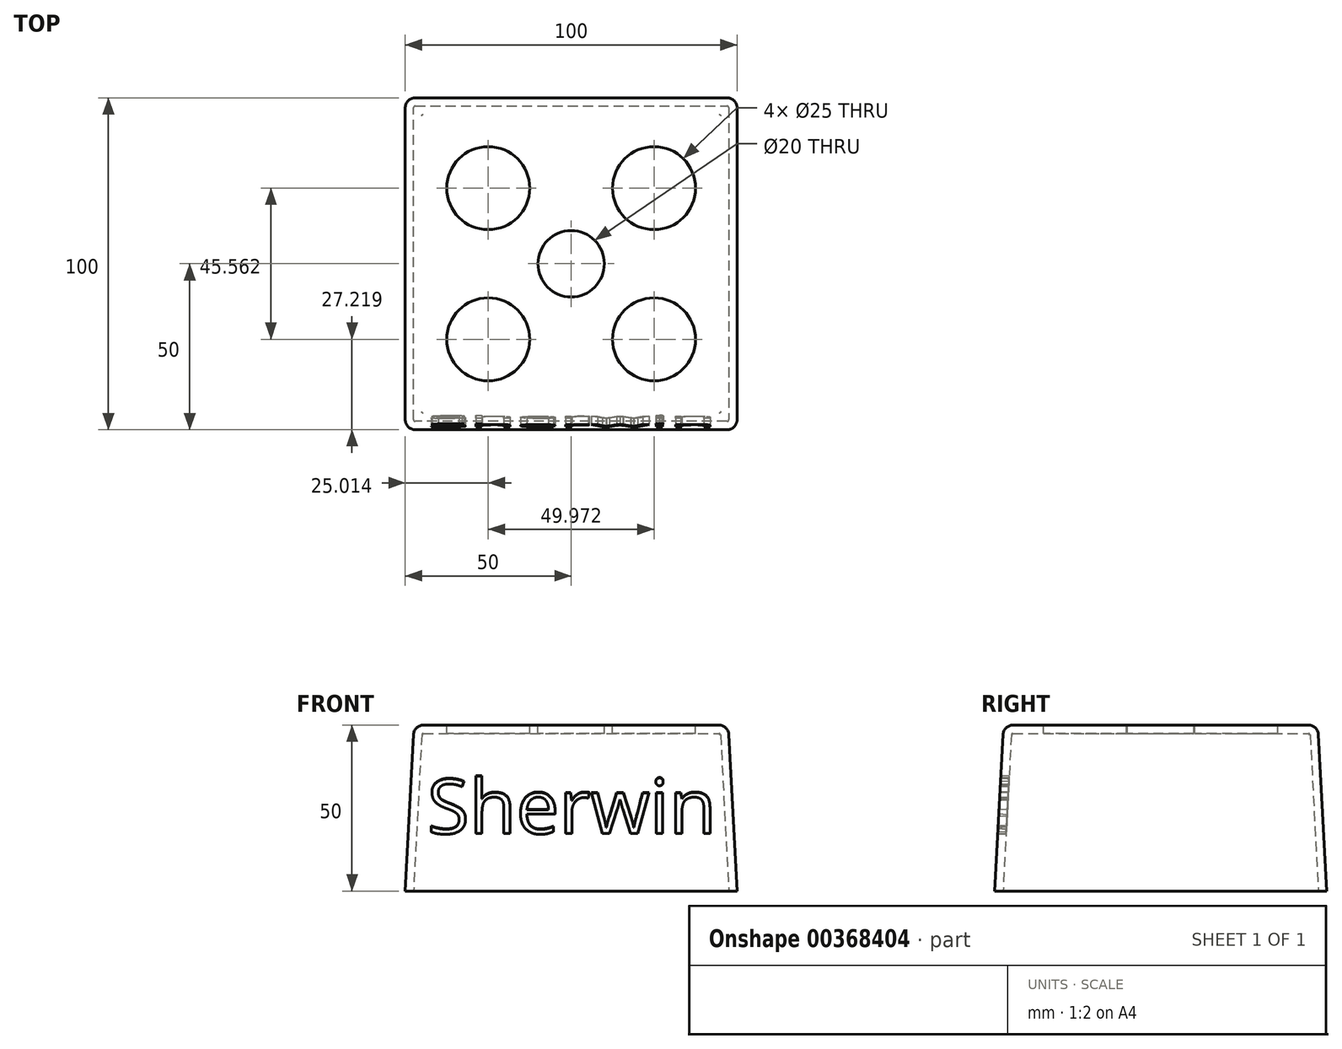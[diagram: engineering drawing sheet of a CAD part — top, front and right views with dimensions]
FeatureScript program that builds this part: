
annotation { "Feature Type Name" : "Feature", "Feature Type Description" : "" }
export const myFeature = defineFeature(function(context is Context, id is Id, definition is map)
    precondition{}
    {
        {
            var Q0;
            Q0=qCreatedBy(makeId("Top.planeOp"),FACE);
            var sketch = newSketch(context, id + "F0", { "sketchPlane" : qUnion([Q0])});
            skLineSegment(sketch, "E0.bottom", {"start": v(0, 0) * mm, "end": v(100, 0) * mm});
            skLineSegment(sketch, "E0.top", {"start": v(0, 100) * mm, "end": v(100, 100) * mm});
            skLineSegment(sketch, "E0.left", {"start": v(0, 0) * mm, "end": v(0, 100) * mm});
            skLineSegment(sketch, "E0.right", {"start": v(100, 0) * mm, "end": v(100, 100) * mm});
            skSolve(sketch);
        }
        {
            var Q0;
            Q0=makeQuery(id+"F0.imprint","IMPRINT",FACE,{"disambiguationData":[TD([[makeQuery(id+"F0.imprint","IMPRINT",EDGE,{"derivedFrom":sQuery(id+"F0.wireOp",EDGE,"E0.bottom")}),1.0]])]});
            extrude(context, id + "F1", {"entities" : qUnion([Q0]), "depth" : 50 * mm, "hasDraft" : true, "draftAngle" : 3 * degree, "draftPullDirection" : true});
        }
        {
            var Q0;
            Q0=makeQuery(id+"F1.opExtrude","SWEPT_EDGE",EDGE,{"disambiguationData":[OSD([sQuery(id+"F0.wireOp",EDGE,"E0.bottom"),sQuery(id+"F0.wireOp",EDGE,"E0.right")])]});
            var Q1;
            Q1=makeQuery(id+"F1.opExtrude","CAP_FACE",FACE,{"disambiguationData":[OSD([sQuery(id+"F0.wireOp",EDGE,"E0.bottom"),sQuery(id+"F0.wireOp",EDGE,"E0.top"),sQuery(id+"F0.wireOp",EDGE,"E0.left"),sQuery(id+"F0.wireOp",EDGE,"E0.right")])],"isStart":false});
            var Q2;
            Q2=makeQuery(id+"F1.opExtrude","SWEPT_EDGE",EDGE,{"disambiguationData":[OSD([sQuery(id+"F0.wireOp",EDGE,"E0.top"),sQuery(id+"F0.wireOp",EDGE,"E0.right")])]});
            var Q3;
            Q3=makeQuery(id+"F1.opExtrude","SWEPT_EDGE",EDGE,{"disambiguationData":[OSD([sQuery(id+"F0.wireOp",EDGE,"E0.bottom"),sQuery(id+"F0.wireOp",EDGE,"E0.left")])]});
            var Q4;
            Q4=makeQuery(id+"F1.opExtrude","SWEPT_EDGE",EDGE,{"disambiguationData":[OSD([sQuery(id+"F0.wireOp",EDGE,"E0.top"),sQuery(id+"F0.wireOp",EDGE,"E0.left")])]});
            fillet(context, id + "F2", {"entities" : qUnion([Q0, Q1, Q2, Q3, Q4]), "radius" : 3 * mm, "tangentPropagation" : true, "allowEdgeOverflow" : false});
        }
        {
            var Q0;
            Q0=makeQuery(id+"F1.opExtrude","CAP_FACE",FACE,{"disambiguationData":[OSD([sQuery(id+"F0.wireOp",EDGE,"E0.bottom"),sQuery(id+"F0.wireOp",EDGE,"E0.top"),sQuery(id+"F0.wireOp",EDGE,"E0.left"),sQuery(id+"F0.wireOp",EDGE,"E0.right")])],"isStart":true});
            shell(context, id + "F3", {"entities" : qUnion([Q0]), "thickness" : 2.5 * mm});
        }
        {
            var Q0;
            Q0=makeQuery(id+"F1.opExtrude","CAP_FACE",FACE,{"disambiguationData":[OSD([sQuery(id+"F0.wireOp",EDGE,"E0.bottom"),sQuery(id+"F0.wireOp",EDGE,"E0.top"),sQuery(id+"F0.wireOp",EDGE,"E0.left"),sQuery(id+"F0.wireOp",EDGE,"E0.right")])],"isStart":false});
            var sketch = newSketch(context, id + "F4", { "sketchPlane" : qUnion([Q0])});
            skCircle(sketch, "E1", {"center": v(50, 50) * mm, "radius": 10 * mm});
            skPoint(sketch, "E1.centerSnap0", {"position": v(5.47, 50) * mm});
            skPoint(sketch, "E1.centerSnap1", {"position": v(50, 94.53) * mm});
            skLineSegment(sketch, "E2", {"start": v(5.47, 50) * mm, "end": v(94.53, 50) * mm, "construction": true});
            skLineSegment(sketch, "E3", {"start": v(50, 94.53) * mm, "end": v(50, 5.47) * mm, "construction": true});
            skCircle(sketch, "E4", {"center": v(25.01, 72.78) * mm, "radius": 12.5 * mm});
            skCircle(sketch, "E5", {"center": v(25.01, 27.22) * mm, "radius": 12.5 * mm});
            skCircle(sketch, "E6", {"center": v(74.99, 27.22) * mm, "radius": 12.5 * mm});
            skCircle(sketch, "E7", {"center": v(74.99, 72.78) * mm, "radius": 12.5 * mm});
            skCircle(sketch, "E8", {"center": v(23, 50) * mm, "radius": 5 * mm});
            skSolve(sketch);
        }
        {
            var Q0;
            Q0=makeQuery(id+"F4.imprint","IMPRINT",FACE,{"disambiguationData":[TD([[makeQuery(id+"F4.imprint","IMPRINT",EDGE,{"derivedFrom":sQuery(id+"F4.wireOp",EDGE,"E1")}),1.0]])]});
            extrude(context, id + "F5", {"entities" : qUnion([Q0]), "operationType" : NewBodyOperationType.REMOVE, "oppositeDirection" : true, "depth" : 3 * mm});
        }
        {
            var Q0;
            Q0=makeQuery(id+"F4.imprint","IMPRINT",FACE,{"disambiguationData":[TD([[makeQuery(id+"F4.imprint","IMPRINT",EDGE,{"derivedFrom":sQuery(id+"F4.wireOp",EDGE,"E5")}),1.0]])]});
            var Q1;
            Q1=makeQuery(id+"F4.imprint","IMPRINT",FACE,{"disambiguationData":[TD([[makeQuery(id+"F4.imprint","IMPRINT",EDGE,{"derivedFrom":sQuery(id+"F4.wireOp",EDGE,"E7")}),1.0]])]});
            var Q2;
            Q2=makeQuery(id+"F4.imprint","IMPRINT",FACE,{"disambiguationData":[TD([[makeQuery(id+"F4.imprint","IMPRINT",EDGE,{"derivedFrom":sQuery(id+"F4.wireOp",EDGE,"E6")}),1.0]])]});
            var Q3;
            Q3=makeQuery(id+"F4.imprint","IMPRINT",FACE,{"disambiguationData":[TD([[makeQuery(id+"F4.imprint","IMPRINT",EDGE,{"derivedFrom":sQuery(id+"F4.wireOp",EDGE,"E4")}),1.0]])]});
            extrude(context, id + "F6", {"entities" : qUnion([Q0, Q1, Q2, Q3]), "operationType" : NewBodyOperationType.REMOVE, "oppositeDirection" : true, "depth" : 3 * mm});
        }
        {
            var Q0;
            Q0=makeQuery(id+"F1.opExtrude","SWEPT_FACE",FACE,{"disambiguationData":[OSD([sQuery(id+"F0.wireOp",EDGE,"E0.bottom")])]});
            var sketch = newSketch(context, id + "F7", { "sketchPlane" : qUnion([Q0])});
            skText(sketch, "E9", { "text": "Sherwin", "fontName": "OpenSans-Regular.ttf"});
            skLineSegment(sketch, "E10.0", {"start": v(5.47, 47.22) * mm, "end": v(3, 0) * mm});
            skLineSegment(sketch, "E10.1", {"start": v(97, 0) * mm, "end": v(94.53, 47.22) * mm});
            const initialGuessF7  = {"E9": [0.00662, 0.01733, 1, 0, 0.0166]};
            skSetInitialGuess(sketch, initialGuessF7);
            skSolve(sketch);
        }
        {
            var Q0;
            Q0=makeQuery(id+"F7.imprint","IMPRINT",FACE,{"disambiguationData":[TD([[makeQuery(id+"F7.imprint","IMPRINT",EDGE,{"derivedFrom":sQuery(id+"F7.wireOp",EDGE,"E9.sketch_text.stroke-75")}),-1.0]])]});
            var Q1;
            Q1 = qSketchRegion(id + "F7", true);
            var Q2;
            Q2=makeQuery(id+"F7.imprint","IMPRINT",FACE,{"disambiguationData":[TD([[makeQuery(id+"F7.imprint","IMPRINT",EDGE,{"derivedFrom":sQuery(id+"F7.wireOp",EDGE,"E9.sketch_text.stroke-0")}),-1.0]])]});
            var Q3;
            Q3=makeQuery(id+"F7.imprint","IMPRINT",FACE,{"disambiguationData":[TD([[makeQuery(id+"F7.imprint","IMPRINT",EDGE,{"derivedFrom":sQuery(id+"F7.wireOp",EDGE,"E9.sketch_text.stroke-98")}),-1.0]])]});
            var Q4;
            Q4=makeQuery(id+"F7.imprint","IMPRINT",FACE,{"disambiguationData":[TD([[makeQuery(id+"F7.imprint","IMPRINT",EDGE,{"derivedFrom":sQuery(id+"F7.wireOp",EDGE,"E9.sketch_text.stroke-62")}),-1.0]])]});
            var Q5;
            Q5=makeQuery(id+"F7.imprint","IMPRINT",FACE,{"disambiguationData":[TD([[makeQuery(id+"F7.imprint","IMPRINT",EDGE,{"derivedFrom":sQuery(id+"F7.wireOp",EDGE,"E9.sketch_text.stroke-43")}),-1.0]])]});
            var Q6;
            Q6=makeQuery(id+"F7.imprint","IMPRINT",FACE,{"disambiguationData":[TD([[makeQuery(id+"F7.imprint","IMPRINT",EDGE,{"derivedFrom":sQuery(id+"F7.wireOp",EDGE,"E9.sketch_text.stroke-25")}),-1.0]])]});
            var Q7;
            Q7=makeQuery(id+"F7.imprint","IMPRINT",FACE,{"disambiguationData":[TD([[makeQuery(id+"F7.imprint","IMPRINT",EDGE,{"derivedFrom":sQuery(id+"F7.wireOp",EDGE,"E9.sketch_text.stroke-110")}),-1.0]])]});
            extrude(context, id + "F8", {"entities" : qUnion([Q0, Q1, Q2, Q3, Q4, Q5, Q6, Q7]), "operationType" : NewBodyOperationType.REMOVE, "oppositeDirection" : true, "depth" : 3 * mm});
        }
    });
